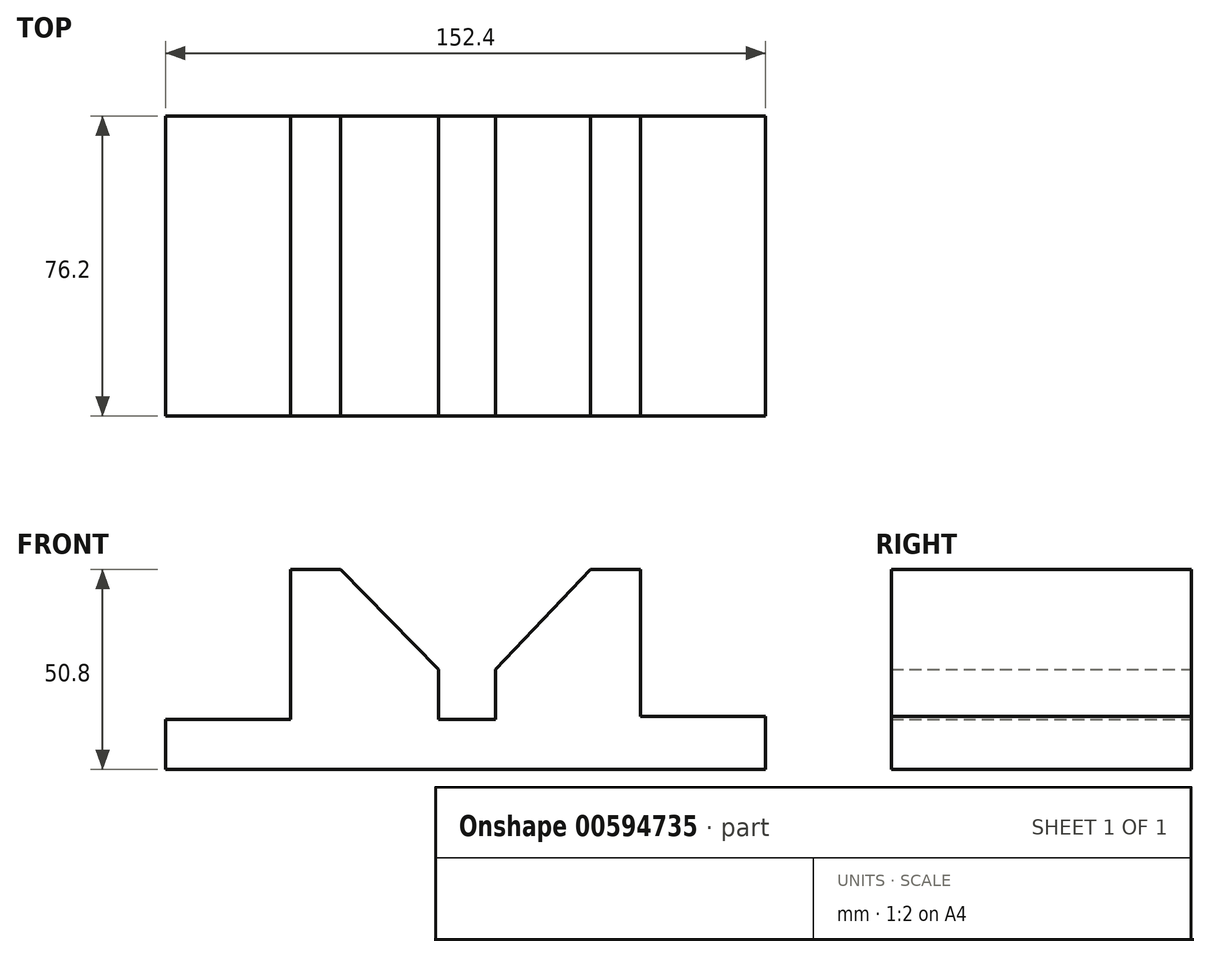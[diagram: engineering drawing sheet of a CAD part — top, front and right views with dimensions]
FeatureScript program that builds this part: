
annotation { "Feature Type Name" : "Feature", "Feature Type Description" : "" }
export const myFeature = defineFeature(function(context is Context, id is Id, definition is map)
    precondition{}
    {
        {
            var Q0;
            Q0=qCreatedBy(makeId("Front.planeOp"),FACE);
            var sketch = newSketch(context, id + "F0", { "sketchPlane" : qUnion([Q0])});
            skLineSegment(sketch, "E0.bottom", {"start": v(0, 0) * mm, "end": v(152.4, 0) * mm});
            skLineSegment(sketch, "E1", {"start": v(0, 0) * mm, "end": v(0, 12.7) * mm});
            skLineSegment(sketch, "E2", {"start": v(0, 12.7) * mm, "end": v(31.75, 12.7) * mm});
            skLineSegment(sketch, "E3", {"start": v(31.75, 12.7) * mm, "end": v(31.75, 50.8) * mm});
            skLineSegment(sketch, "E4", {"start": v(31.75, 50.8) * mm, "end": v(44.45, 50.8) * mm});
            skLineSegment(sketch, "E5", {"start": v(44.45, 50.8) * mm, "end": v(69.28, 50.8) * mm});
            skLineSegment(sketch, "E6", {"start": v(69.28, 12.7) * mm, "end": v(83.82, 12.7) * mm});
            skLineSegment(sketch, "E7", {"start": v(83.82, 12.7) * mm, "end": v(83.82, 25.4) * mm});
            skLineSegment(sketch, "E8", {"start": v(69.28, 12.7) * mm, "end": v(69.28, 25.4) * mm});
            skLineSegment(sketch, "E9", {"start": v(69.28, 25.4) * mm, "end": v(44.45, 50.8) * mm});
            skLineSegment(sketch, "E10", {"start": v(120.65, 25.4) * mm, "end": v(120.65, 50.8) * mm});
            skLineSegment(sketch, "E11", {"start": v(120.65, 50.8) * mm, "end": v(107.95, 50.8) * mm});
            skLineSegment(sketch, "E12", {"start": v(107.95, 50.8) * mm, "end": v(83.82, 25.4) * mm});
            skLineSegment(sketch, "E13", {"start": v(107.95, 50.8) * mm, "end": v(120.65, 50.8) * mm});
            skLineSegment(sketch, "E14", {"start": v(120.65, 25.4) * mm, "end": v(120.65, 13.42) * mm});
            skLineSegment(sketch, "E15", {"start": v(120.65, 13.42) * mm, "end": v(152.4, 13.42) * mm});
            skLineSegment(sketch, "E16", {"start": v(152.4, 13.42) * mm, "end": v(152.4, 0) * mm});
            skSolve(sketch);
        }
        {
            var Q0;
            Q0 = qSketchRegion(id + "F0", true);
            extrude(context, id + "F1", {"entities" : qUnion([Q0]), "depth" : 76.2 * mm, "offsetDistance" : 25.4 * mm});
        }
    });
